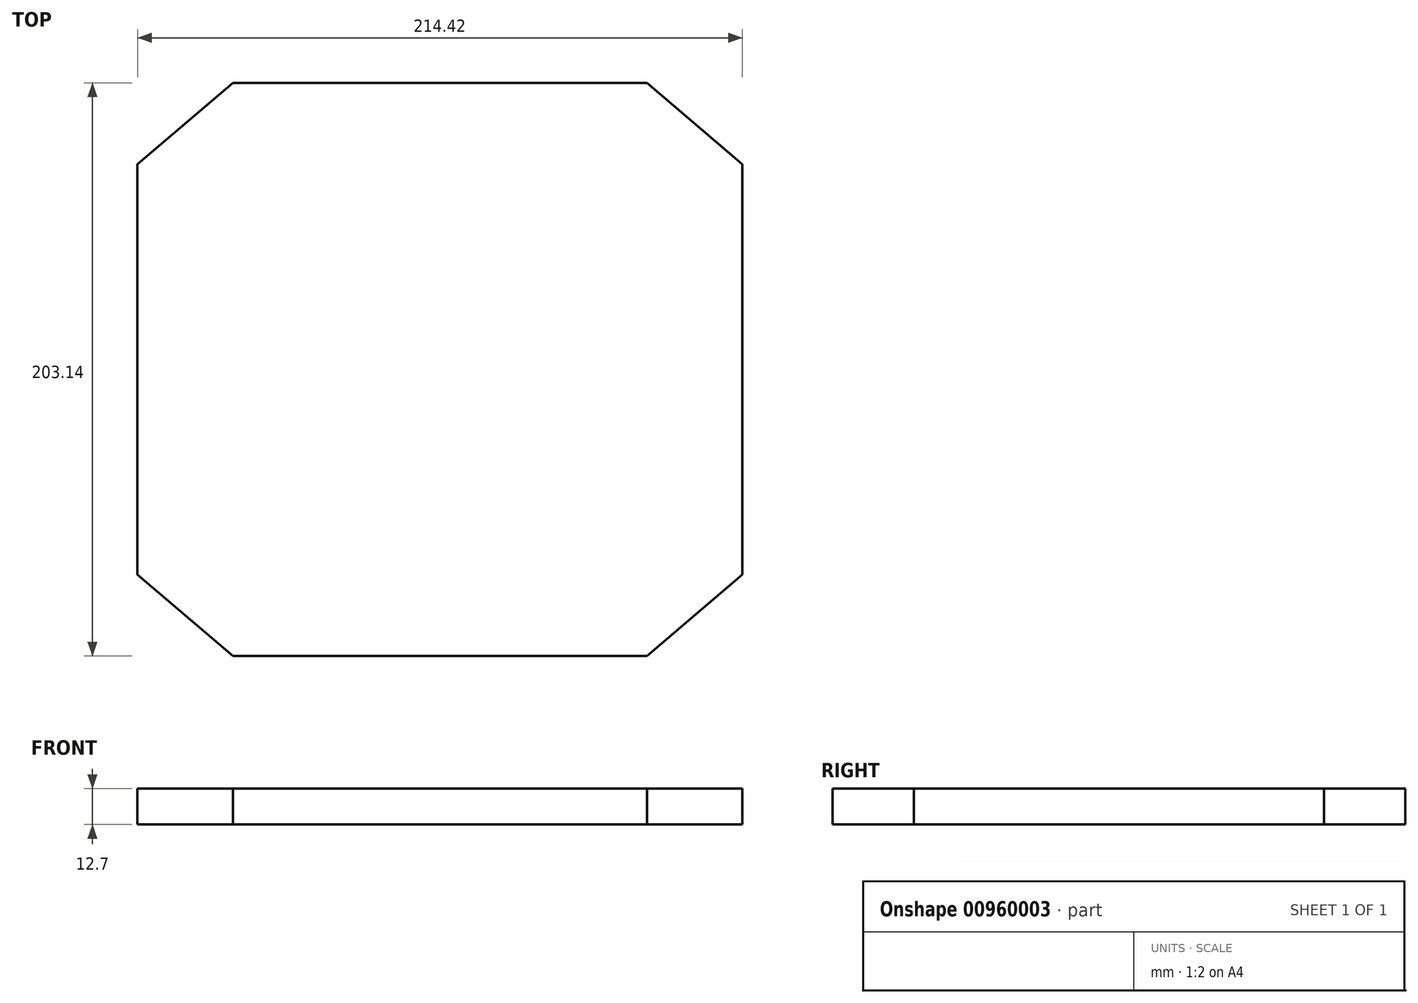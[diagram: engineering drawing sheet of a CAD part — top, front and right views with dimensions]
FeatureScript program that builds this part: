
annotation { "Feature Type Name" : "Feature", "Feature Type Description" : "" }
export const myFeature = defineFeature(function(context is Context, id is Id, definition is map)
    precondition{}
    {
        {
            var Q0;
            Q0=qCreatedBy(makeId("Top.planeOp"),FACE);
            var sketch = newSketch(context, id + "F0", { "sketchPlane" : qUnion([Q0])});
            skLineSegment(sketch, "E0.0", {"start": v(-7.62, -3.51) * mm, "end": v(-41.44, 25.37) * mm});
            skLineSegment(sketch, "E0.1", {"start": v(-7.62, -148.89) * mm, "end": v(-7.62, -3.51) * mm});
            skLineSegment(sketch, "E0.2", {"start": v(-41.44, 25.37) * mm, "end": v(-188.22, 25.37) * mm});
            skLineSegment(sketch, "E0.3", {"start": v(-41.44, -177.77) * mm, "end": v(-7.62, -148.89) * mm});
            skLineSegment(sketch, "E0.4", {"start": v(-188.22, 25.37) * mm, "end": v(-222.04, -3.51) * mm});
            skLineSegment(sketch, "E0.5", {"start": v(-222.04, -3.51) * mm, "end": v(-222.04, -148.89) * mm});
            skLineSegment(sketch, "E0.6", {"start": v(-222.04, -148.89) * mm, "end": v(-188.22, -177.77) * mm});
            skLineSegment(sketch, "E0.7", {"start": v(-188.22, -177.77) * mm, "end": v(-41.44, -177.77) * mm});
            skSolve(sketch);
        }
        {
            var Q0;
            Q0=qSketchRegion(id+"F0",true);
            extrude(context, id + "F1", {"entities" : qUnion([Q0]), "depth" : 12.7 * mm, "offsetDistance" : 25.4 * mm});
        }
    });
